# Revit family: 220-35 OPENING ROOF))
name_source: partatom
category: Generic Models
revit_build: Autodesk Revit 2018 (Build: 20190510_1515(x64)
units: mm (PartAtom-declared; Revit-internal decimal feet)

## family parameters
Always vertical = Yes
Can host rebar = No
Cut with Voids When Loaded = No
Part Type = Normal
Room Calculation Point = No
Round Connector Dimension = Use Diameter
Shared = No
Work Plane-Based = No

## types (1)
- 220-35 OPENING ROOF))
    185 GUTTER = <By Category>
    220-35 BLADE AND END CAP = <By Category>
    BEAM = <By Category>
    BEAM AND POST THICKNESS LIMITS = 3 mm  [stored 0.00984252 ft]
    BEAM HEIGHT = 250 mm  [stored 0.82021 ft]
    BEAM HEIGHT LIMITS = 250 mm  [stored 0.82021 ft]
    BEAM THICKNESS = 3 mm  [stored 0.00984252 ft]
    BEAM WIDTH = -7000 mm  [stored -22.9659 ft]
    BEAM WIDTH LIMITS = 50 mm  [stored 0.164042 ft]
    DRIVE AND PASSIVE FRAME OFFSET = 22 mm  [stored 0.0721785 ft]
    FLASHING = <By Category>
    HEIGHT = 2200 mm  [stored 7.21785 ft]
    HEIGHT LIMIT = 2200 mm  [stored 7.21785 ft]
    LENGTH (SPAN SIDE) = 2500 mm  [stored 8.2021 ft]
    LENGTH LIMIT = 2500 mm  [stored 8.2021 ft]
    LOUVRE ANGLE = 0.00°
    LOUVRE ROTATION LIMIT = 0.00°
    OFFSET LIMITS = 22 mm  [stored 0.0721785 ft]
    PASSIVE AND DRIVE FRAME = <By Category>
    PITCH = 1.00°
    POST = <By Category>
    POST LENGTH = 100 mm  [stored 0.328084 ft]
    POST LENGTH LIMITS = 100 mm  [stored 0.328084 ft]
    POST THICKNESS = 3 mm  [stored 0.00984252 ft]
    POST WIDTH = 100 mm  [stored 0.328084 ft]
    POST WIDTH LIMITS = 100 mm  [stored 0.328084 ft]
    SPACING = 205 mm  [stored 0.672572 ft]
    VISABLE 180-30 SLIMLINE LOUVRE BLADE = Yes
    VISABLE 185 GUTTER = Yes
    VISABLE BEAM = Yes
    VISABLE FLASHING = Yes
    VISABLE PASSIVE AND DRIVE FRAME = Yes
    VISABLE POST = Yes
    WIDTH (PIVOT SIDE) = 3234 mm  [stored 10.6102 ft]
    WIDTH LIMIT = 3234 mm  [stored 10.6102 ft]

note: [stored X ft] marks values corroborated as IEEE doubles in the binary element streams (Revit-internal decimal feet)

## geometry (parser evidence)
native form markers: Sweep x28
no freeform markers — native parametric forms only
